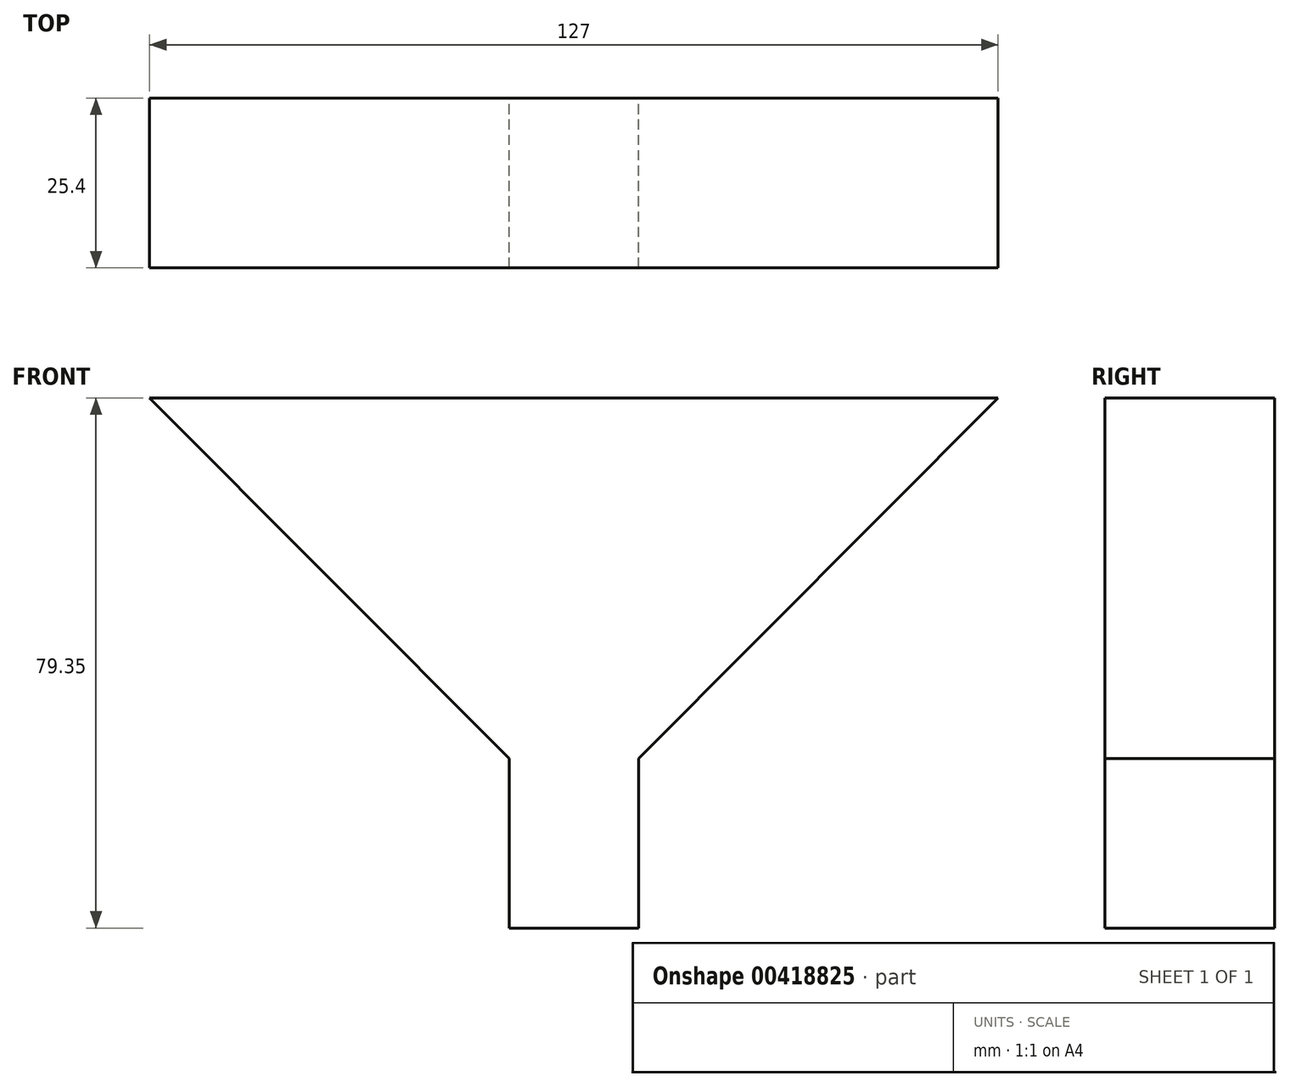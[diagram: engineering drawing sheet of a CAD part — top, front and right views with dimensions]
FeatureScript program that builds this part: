
annotation { "Feature Type Name" : "Feature", "Feature Type Description" : "" }
export const myFeature = defineFeature(function(context is Context, id is Id, definition is map)
    precondition{}
    {
        {
            var Q0;
            Q0=qCreatedBy(makeId("Front.planeOp"),FACE);
            var sketch = newSketch(context, id + "F0", { "sketchPlane" : qUnion([Q0])});
            skLineSegment(sketch, "E0", {"start": v(0, 0) * mm, "end": v(0, 25.4) * mm});
            skLineSegment(sketch, "E1", {"start": v(0, 25.4) * mm, "end": v(53.81, 79.35) * mm});
            skLineSegment(sketch, "E2", {"start": v(53.81, 79.35) * mm, "end": v(-73.19, 79.35) * mm});
            skLineSegment(sketch, "E3", {"start": v(-73.19, 79.35) * mm, "end": v(-19.38, 25.4) * mm});
            skLineSegment(sketch, "E4", {"start": v(-19.38, 25.4) * mm, "end": v(-19.38, 0) * mm});
            skLineSegment(sketch, "E5", {"start": v(-19.38, 0) * mm, "end": v(0, 0) * mm});
            skSolve(sketch);
        }
        {
            var Q0;
            Q0 = qSketchRegion(id + "F0", true);
            extrude(context, id + "F1", {"entities" : qUnion([Q0]), "depth" : 25.4 * mm});
        }
    });
